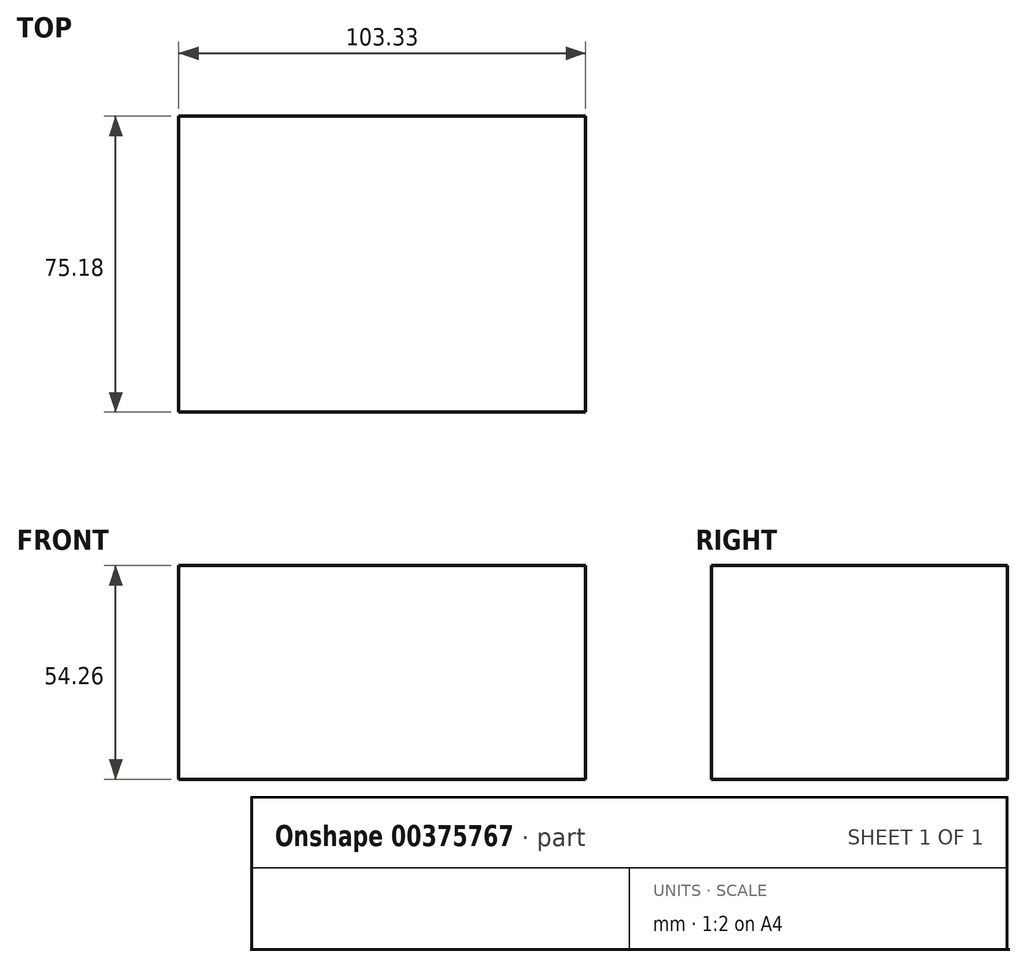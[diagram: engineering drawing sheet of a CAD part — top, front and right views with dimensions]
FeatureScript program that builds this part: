
annotation { "Feature Type Name" : "Feature", "Feature Type Description" : "" }
export const myFeature = defineFeature(function(context is Context, id is Id, definition is map)
    precondition{}
    {
        {
            var Q0;
            Q0=qCreatedBy(makeId("Front.planeOp"),FACE);
            var sketch = newSketch(context, id + "F0", { "sketchPlane" : qUnion([Q0])});
            skLineSegment(sketch, "E0.bottom", {"start": v(-51.82, 33.99) * mm, "end": v(12.8, 33.99) * mm});
            skLineSegment(sketch, "E0.top", {"start": v(-51.82, -20.27) * mm, "end": v(12.8, -20.27) * mm});
            skLineSegment(sketch, "E0.left", {"start": v(-51.82, 33.99) * mm, "end": v(-51.82, -20.27) * mm});
            skLineSegment(sketch, "E0.right", {"start": v(12.8, 33.99) * mm, "end": v(12.8, -20.27) * mm});
            skLineSegment(sketch, "E1.bottom", {"start": v(12.8, 33.99) * mm, "end": v(51.51, 33.99) * mm});
            skLineSegment(sketch, "E1.top", {"start": v(12.8, 8.69) * mm, "end": v(51.51, 8.69) * mm});
            skLineSegment(sketch, "E1.left", {"start": v(12.8, 33.99) * mm, "end": v(12.8, 8.69) * mm});
            skLineSegment(sketch, "E1.right", {"start": v(51.51, 33.99) * mm, "end": v(51.51, 8.69) * mm});
            skLineSegment(sketch, "E2.bottom", {"start": v(51.51, 8.69) * mm, "end": v(12.8, 8.69) * mm});
            skLineSegment(sketch, "E2.top", {"start": v(51.51, -20.27) * mm, "end": v(12.8, -20.27) * mm});
            skLineSegment(sketch, "E2.left", {"start": v(51.51, 8.69) * mm, "end": v(51.51, -20.27) * mm});
            skLineSegment(sketch, "E2.right", {"start": v(12.8, 8.69) * mm, "end": v(12.8, -20.27) * mm});
            skSolve(sketch);
        }
        {
            var Q0;
            Q0 = qSketchRegion(id + "F0", true);
            extrude(context, id + "F1", {"entities" : qUnion([Q0]), "oppositeDirection" : true, "depth" : 75.18 * mm});
        }
    });
